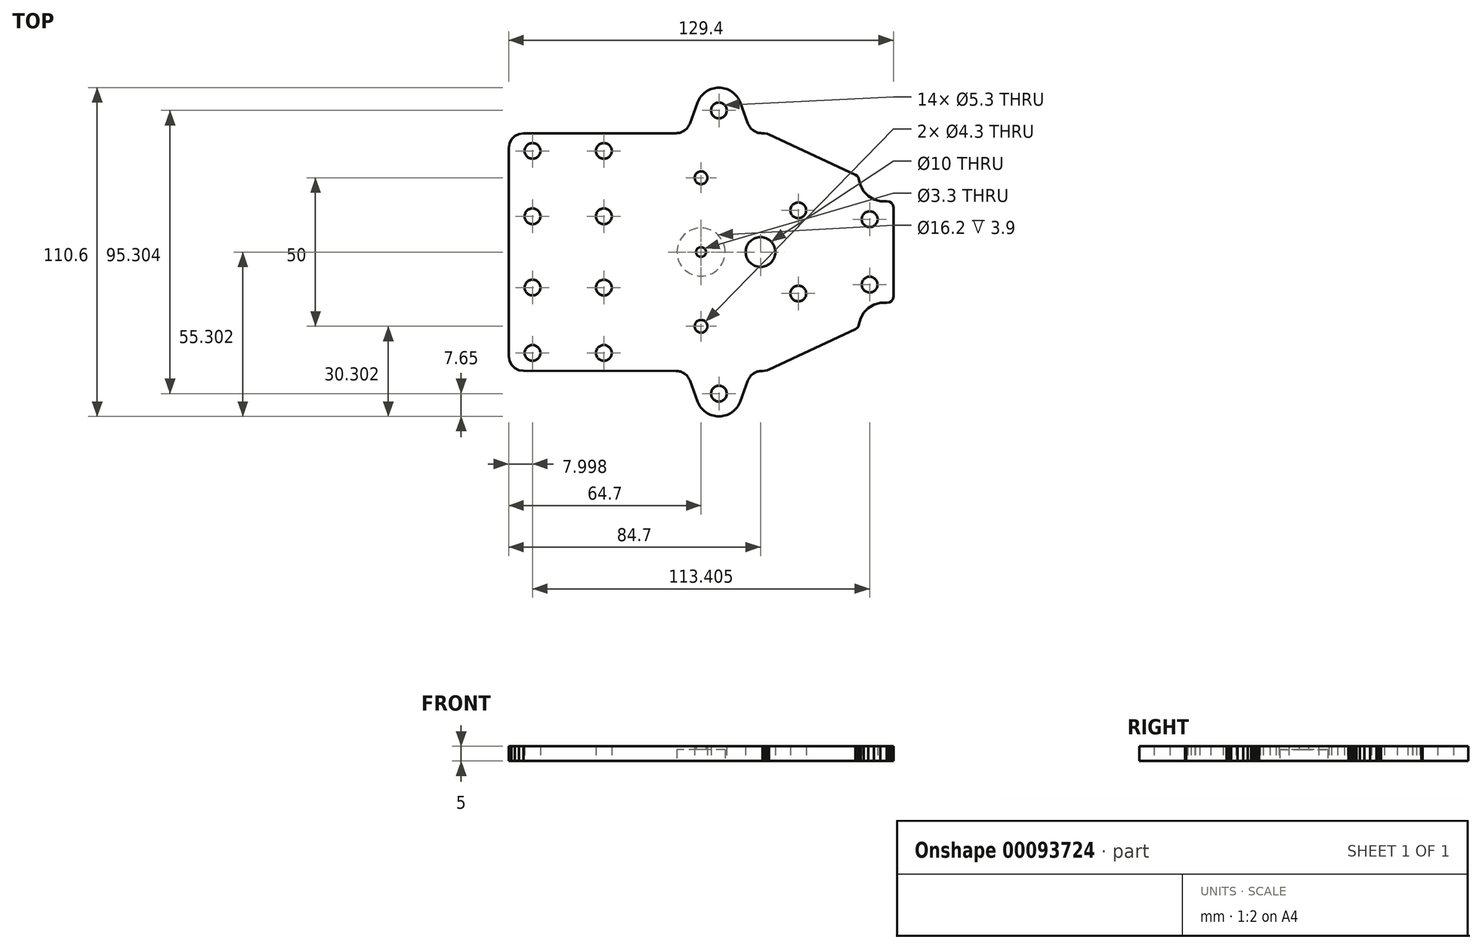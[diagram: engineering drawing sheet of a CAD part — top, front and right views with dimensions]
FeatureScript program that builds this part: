
annotation { "Feature Type Name" : "Feature", "Feature Type Description" : "" }
export const myFeature = defineFeature(function(context is Context, id is Id, definition is map)
    precondition{}
    {
        {
            var Q0;
            Q0=qCreatedBy(makeId("Top.planeOp"),FACE);
            var sketch = newSketch(context, id + "F0", { "sketchPlane" : qUnion([Q0])});
            skLineSegment(sketch, "E0", {"start": v(-58.76, 13.43) * mm, "end": v(-57.86, 14.22) * mm});
            skLineSegment(sketch, "E1", {"start": v(-57.86, 14.22) * mm, "end": v(-56.7, 14.5) * mm});
            skLineSegment(sketch, "E2", {"start": v(-56.7, 14.5) * mm, "end": v(-55.54, 14.21) * mm});
            skLineSegment(sketch, "E3", {"start": v(-55.54, 14.21) * mm, "end": v(-54.64, 13.42) * mm});
            skLineSegment(sketch, "E4", {"start": v(-54.64, 13.42) * mm, "end": v(-54.22, 12.3) * mm});
            skLineSegment(sketch, "E5", {"start": v(-54.22, 12.3) * mm, "end": v(-54.37, 11.12) * mm});
            skLineSegment(sketch, "E6", {"start": v(-54.37, 11.12) * mm, "end": v(-55.04, 10.13) * mm});
            skLineSegment(sketch, "E7", {"start": v(-55.04, 10.13) * mm, "end": v(-56.1, 9.57) * mm});
            skLineSegment(sketch, "E8", {"start": v(-56.1, 9.57) * mm, "end": v(-57.3, 9.58) * mm});
            skLineSegment(sketch, "E9", {"start": v(-57.3, 9.58) * mm, "end": v(-58.36, 10.13) * mm});
            skLineSegment(sketch, "E10", {"start": v(-58.36, 10.13) * mm, "end": v(-59.04, 11.12) * mm});
            skLineSegment(sketch, "E11", {"start": v(-59.04, 11.12) * mm, "end": v(-59.18, 12.3) * mm});
            skLineSegment(sketch, "E12", {"start": v(-59.18, 12.3) * mm, "end": v(-58.76, 13.43) * mm});
            skLineSegment(sketch, "E13", {"start": v(35.04, -14.88) * mm, "end": v(34.36, -15.87) * mm});
            skLineSegment(sketch, "E14", {"start": v(34.36, -15.87) * mm, "end": v(33.3, -16.43) * mm});
            skLineSegment(sketch, "E15", {"start": v(33.3, -16.43) * mm, "end": v(32.1, -16.42) * mm});
            skLineSegment(sketch, "E16", {"start": v(32.1, -16.42) * mm, "end": v(31.04, -15.87) * mm});
            skLineSegment(sketch, "E17", {"start": v(31.04, -15.87) * mm, "end": v(30.36, -14.89) * mm});
            skLineSegment(sketch, "E18", {"start": v(30.36, -14.89) * mm, "end": v(30.22, -13.7) * mm});
            skLineSegment(sketch, "E19", {"start": v(30.22, -13.7) * mm, "end": v(30.64, -12.57) * mm});
            skLineSegment(sketch, "E20", {"start": v(30.64, -12.57) * mm, "end": v(31.54, -11.79) * mm});
            skLineSegment(sketch, "E21", {"start": v(31.54, -11.79) * mm, "end": v(32.7, -11.5) * mm});
            skLineSegment(sketch, "E22", {"start": v(32.7, -11.5) * mm, "end": v(33.86, -11.79) * mm});
            skLineSegment(sketch, "E23", {"start": v(33.86, -11.79) * mm, "end": v(34.76, -12.58) * mm});
            skLineSegment(sketch, "E24", {"start": v(34.76, -12.58) * mm, "end": v(35.18, -13.7) * mm});
            skLineSegment(sketch, "E25", {"start": v(35.18, -13.7) * mm, "end": v(35.04, -14.88) * mm});
            skLineSegment(sketch, "E26", {"start": v(54.72, -20.36) * mm, "end": v(56.27, -18.8) * mm});
            skLineSegment(sketch, "E27", {"start": v(56.27, -18.8) * mm, "end": v(58.16, -17.68) * mm});
            skLineSegment(sketch, "E28", {"start": v(58.16, -17.68) * mm, "end": v(60.27, -17.08) * mm});
            skLineSegment(sketch, "E29", {"start": v(60.27, -17.08) * mm, "end": v(62.47, -17.06) * mm});
            skLineSegment(sketch, "E30", {"start": v(62.47, -17.06) * mm, "end": v(63.3, -16.97) * mm});
            skLineSegment(sketch, "E31", {"start": v(63.3, -16.97) * mm, "end": v(64.03, -16.56) * mm});
            skLineSegment(sketch, "E32", {"start": v(64.03, -16.56) * mm, "end": v(64.52, -15.88) * mm});
            skLineSegment(sketch, "E33", {"start": v(64.52, -15.88) * mm, "end": v(64.7, -15.07) * mm});
            skLineSegment(sketch, "E34", {"start": v(64.7, -15.07) * mm, "end": v(64.7, 15.07) * mm});
            skLineSegment(sketch, "E35", {"start": v(64.7, 15.07) * mm, "end": v(64.53, 15.9) * mm});
            skLineSegment(sketch, "E36", {"start": v(64.53, 15.9) * mm, "end": v(64.03, 16.57) * mm});
            skLineSegment(sketch, "E37", {"start": v(64.03, 16.57) * mm, "end": v(63.3, 16.98) * mm});
            skLineSegment(sketch, "E38", {"start": v(63.3, 16.98) * mm, "end": v(62.47, 17.06) * mm});
            skLineSegment(sketch, "E39", {"start": v(62.47, 17.06) * mm, "end": v(60.27, 17.08) * mm});
            skLineSegment(sketch, "E40", {"start": v(60.27, 17.08) * mm, "end": v(58.15, 17.68) * mm});
            skLineSegment(sketch, "E41", {"start": v(58.15, 17.68) * mm, "end": v(56.26, 18.8) * mm});
            skLineSegment(sketch, "E42", {"start": v(56.26, 18.8) * mm, "end": v(54.72, 20.36) * mm});
            skLineSegment(sketch, "E43", {"start": v(54.72, 20.36) * mm, "end": v(53.64, 22.28) * mm});
            skLineSegment(sketch, "E44", {"start": v(53.64, 22.28) * mm, "end": v(53.07, 24.4) * mm});
            skLineSegment(sketch, "E45", {"start": v(53.07, 24.4) * mm, "end": v(52.88, 25.04) * mm});
            skLineSegment(sketch, "E46", {"start": v(52.88, 25.04) * mm, "end": v(52.48, 25.58) * mm});
            skLineSegment(sketch, "E47", {"start": v(52.48, 25.58) * mm, "end": v(51.93, 25.95) * mm});
            skLineSegment(sketch, "E48", {"start": v(51.93, 25.95) * mm, "end": v(22.81, 39.53) * mm});
            skLineSegment(sketch, "E49", {"start": v(22.81, 39.53) * mm, "end": v(22.14, 39.8) * mm});
            skLineSegment(sketch, "E50", {"start": v(22.14, 39.8) * mm, "end": v(21.43, 39.95) * mm});
            skLineSegment(sketch, "E51", {"start": v(21.43, 39.95) * mm, "end": v(20.7, 40) * mm});
            skLineSegment(sketch, "E52", {"start": v(20.7, 40) * mm, "end": v(-59.7, 40) * mm});
            skLineSegment(sketch, "E53", {"start": v(-59.7, 40) * mm, "end": v(-61.24, 39.76) * mm});
            skLineSegment(sketch, "E54", {"start": v(-61.24, 39.76) * mm, "end": v(-62.63, 39.05) * mm});
            skLineSegment(sketch, "E55", {"start": v(-62.63, 39.05) * mm, "end": v(-63.75, 37.95) * mm});
            skLineSegment(sketch, "E56", {"start": v(-63.75, 37.95) * mm, "end": v(-64.45, 36.55) * mm});
            skLineSegment(sketch, "E57", {"start": v(-64.45, 36.55) * mm, "end": v(-64.7, 35) * mm});
            skLineSegment(sketch, "E58", {"start": v(-64.7, 35) * mm, "end": v(-64.7, -35) * mm});
            skLineSegment(sketch, "E59", {"start": v(-64.7, -35) * mm, "end": v(-64.45, -36.54) * mm});
            skLineSegment(sketch, "E60", {"start": v(-64.45, -36.54) * mm, "end": v(-63.75, -37.93) * mm});
            skLineSegment(sketch, "E61", {"start": v(-63.75, -37.93) * mm, "end": v(-62.63, -39.04) * mm});
            skLineSegment(sketch, "E62", {"start": v(-62.63, -39.04) * mm, "end": v(-61.25, -39.75) * mm});
            skLineSegment(sketch, "E63", {"start": v(-61.25, -39.75) * mm, "end": v(-59.7, -40) * mm});
            skLineSegment(sketch, "E64", {"start": v(-59.7, -40) * mm, "end": v(20.7, -40) * mm});
            skLineSegment(sketch, "E65", {"start": v(20.7, -40) * mm, "end": v(21.43, -39.95) * mm});
            skLineSegment(sketch, "E66", {"start": v(21.43, -39.95) * mm, "end": v(22.14, -39.8) * mm});
            skLineSegment(sketch, "E67", {"start": v(22.14, -39.8) * mm, "end": v(22.81, -39.53) * mm});
            skLineSegment(sketch, "E68", {"start": v(22.81, -39.53) * mm, "end": v(51.93, -25.95) * mm});
            skLineSegment(sketch, "E69", {"start": v(51.93, -25.95) * mm, "end": v(52.48, -25.57) * mm});
            skLineSegment(sketch, "E70", {"start": v(52.48, -25.57) * mm, "end": v(52.87, -25.04) * mm});
            skLineSegment(sketch, "E71", {"start": v(52.87, -25.04) * mm, "end": v(53.07, -24.4) * mm});
            skLineSegment(sketch, "E72", {"start": v(53.07, -24.4) * mm, "end": v(53.63, -22.27) * mm});
            skLineSegment(sketch, "E73", {"start": v(53.63, -22.27) * mm, "end": v(54.72, -20.36) * mm});
            skLineSegment(sketch, "E74", {"start": v(54.36, -11.89) * mm, "end": v(54.22, -10.7) * mm});
            skLineSegment(sketch, "E75", {"start": v(54.22, -10.7) * mm, "end": v(54.65, -9.58) * mm});
            skLineSegment(sketch, "E76", {"start": v(54.65, -9.58) * mm, "end": v(55.54, -8.79) * mm});
            skLineSegment(sketch, "E77", {"start": v(55.54, -8.79) * mm, "end": v(56.7, -8.5) * mm});
            skLineSegment(sketch, "E78", {"start": v(56.7, -8.5) * mm, "end": v(57.86, -8.78) * mm});
            skLineSegment(sketch, "E79", {"start": v(57.86, -8.78) * mm, "end": v(58.75, -9.57) * mm});
            skLineSegment(sketch, "E80", {"start": v(58.75, -9.57) * mm, "end": v(59.18, -10.7) * mm});
            skLineSegment(sketch, "E81", {"start": v(59.18, -10.7) * mm, "end": v(59.04, -11.89) * mm});
            skLineSegment(sketch, "E82", {"start": v(59.04, -11.89) * mm, "end": v(58.36, -12.87) * mm});
            skLineSegment(sketch, "E83", {"start": v(58.36, -12.87) * mm, "end": v(57.3, -13.42) * mm});
            skLineSegment(sketch, "E84", {"start": v(57.3, -13.42) * mm, "end": v(56.1, -13.42) * mm});
            skLineSegment(sketch, "E85", {"start": v(56.1, -13.42) * mm, "end": v(55.04, -12.87) * mm});
            skLineSegment(sketch, "E86", {"start": v(55.04, -12.87) * mm, "end": v(54.36, -11.89) * mm});
            skLineSegment(sketch, "E87", {"start": v(-30.64, -32.58) * mm, "end": v(-30.22, -33.7) * mm});
            skLineSegment(sketch, "E88", {"start": v(-30.22, -33.7) * mm, "end": v(-30.36, -34.89) * mm});
            skLineSegment(sketch, "E89", {"start": v(-30.36, -34.89) * mm, "end": v(-31.04, -35.87) * mm});
            skLineSegment(sketch, "E90", {"start": v(-31.04, -35.87) * mm, "end": v(-32.1, -36.43) * mm});
            skLineSegment(sketch, "E91", {"start": v(-32.1, -36.43) * mm, "end": v(-33.3, -36.42) * mm});
            skLineSegment(sketch, "E92", {"start": v(-33.3, -36.42) * mm, "end": v(-34.36, -35.87) * mm});
            skLineSegment(sketch, "E93", {"start": v(-34.36, -35.87) * mm, "end": v(-35.04, -34.88) * mm});
            skLineSegment(sketch, "E94", {"start": v(-35.04, -34.88) * mm, "end": v(-35.18, -33.7) * mm});
            skLineSegment(sketch, "E95", {"start": v(-35.18, -33.7) * mm, "end": v(-34.76, -32.57) * mm});
            skLineSegment(sketch, "E96", {"start": v(-34.76, -32.57) * mm, "end": v(-33.86, -31.79) * mm});
            skLineSegment(sketch, "E97", {"start": v(-33.86, -31.79) * mm, "end": v(-32.7, -31.5) * mm});
            skLineSegment(sketch, "E98", {"start": v(-32.7, -31.5) * mm, "end": v(-31.54, -31.78) * mm});
            skLineSegment(sketch, "E99", {"start": v(-31.54, -31.78) * mm, "end": v(-30.64, -32.58) * mm});
            skLineSegment(sketch, "E100", {"start": v(4.37, -36.83) * mm, "end": v(3.71, -35.87) * mm});
            skLineSegment(sketch, "E101", {"start": v(3.71, -35.87) * mm, "end": v(3.57, -34.7) * mm});
            skLineSegment(sketch, "E102", {"start": v(3.57, -34.7) * mm, "end": v(3.98, -33.6) * mm});
            skLineSegment(sketch, "E103", {"start": v(3.98, -33.6) * mm, "end": v(4.86, -32.83) * mm});
            skLineSegment(sketch, "E104", {"start": v(4.86, -32.83) * mm, "end": v(6, -32.55) * mm});
            skLineSegment(sketch, "E105", {"start": v(6, -32.55) * mm, "end": v(7.14, -32.83) * mm});
            skLineSegment(sketch, "E106", {"start": v(7.14, -32.83) * mm, "end": v(8.02, -33.6) * mm});
            skLineSegment(sketch, "E107", {"start": v(8.02, -33.6) * mm, "end": v(8.43, -34.7) * mm});
            skLineSegment(sketch, "E108", {"start": v(8.43, -34.7) * mm, "end": v(8.29, -35.86) * mm});
            skLineSegment(sketch, "E109", {"start": v(8.29, -35.86) * mm, "end": v(7.62, -36.83) * mm});
            skLineSegment(sketch, "E110", {"start": v(7.62, -36.83) * mm, "end": v(6.58, -37.37) * mm});
            skLineSegment(sketch, "E111", {"start": v(6.58, -37.37) * mm, "end": v(5.4, -37.38) * mm});
            skLineSegment(sketch, "E112", {"start": v(5.4, -37.38) * mm, "end": v(4.37, -36.83) * mm});
            skLineSegment(sketch, "E113", {"start": v(58.36, 9.13) * mm, "end": v(57.3, 8.58) * mm});
            skLineSegment(sketch, "E114", {"start": v(57.3, 8.58) * mm, "end": v(56.1, 8.58) * mm});
            skLineSegment(sketch, "E115", {"start": v(56.1, 8.58) * mm, "end": v(55.04, 9.13) * mm});
            skLineSegment(sketch, "E116", {"start": v(55.04, 9.13) * mm, "end": v(54.36, 10.12) * mm});
            skLineSegment(sketch, "E117", {"start": v(54.36, 10.12) * mm, "end": v(54.21, 11.3) * mm});
            skLineSegment(sketch, "E118", {"start": v(54.21, 11.3) * mm, "end": v(54.64, 12.42) * mm});
            skLineSegment(sketch, "E119", {"start": v(54.64, 12.42) * mm, "end": v(55.54, 13.21) * mm});
            skLineSegment(sketch, "E120", {"start": v(55.54, 13.21) * mm, "end": v(56.7, 13.5) * mm});
            skLineSegment(sketch, "E121", {"start": v(56.7, 13.5) * mm, "end": v(57.86, 13.22) * mm});
            skLineSegment(sketch, "E122", {"start": v(57.86, 13.22) * mm, "end": v(58.75, 12.42) * mm});
            skLineSegment(sketch, "E123", {"start": v(58.75, 12.42) * mm, "end": v(59.18, 11.3) * mm});
            skLineSegment(sketch, "E124", {"start": v(59.18, 11.3) * mm, "end": v(59.03, 10.11) * mm});
            skLineSegment(sketch, "E125", {"start": v(59.03, 10.11) * mm, "end": v(58.36, 9.13) * mm});
            skLineSegment(sketch, "E126", {"start": v(-30.21, 34.3) * mm, "end": v(-30.36, 33.11) * mm});
            skLineSegment(sketch, "E127", {"start": v(-30.36, 33.11) * mm, "end": v(-31.04, 32.13) * mm});
            skLineSegment(sketch, "E128", {"start": v(-31.04, 32.13) * mm, "end": v(-32.1, 31.58) * mm});
            skLineSegment(sketch, "E129", {"start": v(-32.1, 31.58) * mm, "end": v(-33.3, 31.58) * mm});
            skLineSegment(sketch, "E130", {"start": v(-33.3, 31.58) * mm, "end": v(-34.36, 32.13) * mm});
            skLineSegment(sketch, "E131", {"start": v(-34.36, 32.13) * mm, "end": v(-35.03, 33.12) * mm});
            skLineSegment(sketch, "E132", {"start": v(-35.03, 33.12) * mm, "end": v(-35.18, 34.3) * mm});
            skLineSegment(sketch, "E133", {"start": v(-35.18, 34.3) * mm, "end": v(-34.76, 35.42) * mm});
            skLineSegment(sketch, "E134", {"start": v(-34.76, 35.42) * mm, "end": v(-33.86, 36.21) * mm});
            skLineSegment(sketch, "E135", {"start": v(-33.86, 36.21) * mm, "end": v(-32.7, 36.5) * mm});
            skLineSegment(sketch, "E136", {"start": v(-32.7, 36.5) * mm, "end": v(-31.54, 36.21) * mm});
            skLineSegment(sketch, "E137", {"start": v(-31.54, 36.21) * mm, "end": v(-30.64, 35.42) * mm});
            skLineSegment(sketch, "E138", {"start": v(-30.64, 35.42) * mm, "end": v(-30.21, 34.3) * mm});
            skLineSegment(sketch, "E139", {"start": v(3.98, 36.4) * mm, "end": v(4.86, 37.17) * mm});
            skLineSegment(sketch, "E140", {"start": v(4.86, 37.17) * mm, "end": v(6, 37.45) * mm});
            skLineSegment(sketch, "E141", {"start": v(6, 37.45) * mm, "end": v(7.14, 37.17) * mm});
            skLineSegment(sketch, "E142", {"start": v(7.14, 37.17) * mm, "end": v(8.02, 36.39) * mm});
            skLineSegment(sketch, "E143", {"start": v(8.02, 36.39) * mm, "end": v(8.43, 35.3) * mm});
            skLineSegment(sketch, "E144", {"start": v(8.43, 35.3) * mm, "end": v(8.3, 34.13) * mm});
            skLineSegment(sketch, "E145", {"start": v(8.3, 34.13) * mm, "end": v(7.62, 33.17) * mm});
            skLineSegment(sketch, "E146", {"start": v(7.62, 33.17) * mm, "end": v(6.58, 32.63) * mm});
            skLineSegment(sketch, "E147", {"start": v(6.58, 32.63) * mm, "end": v(5.4, 32.62) * mm});
            skLineSegment(sketch, "E148", {"start": v(5.4, 32.62) * mm, "end": v(4.37, 33.17) * mm});
            skLineSegment(sketch, "E149", {"start": v(4.37, 33.17) * mm, "end": v(3.7, 34.13) * mm});
            skLineSegment(sketch, "E150", {"start": v(3.7, 34.13) * mm, "end": v(3.57, 35.3) * mm});
            skLineSegment(sketch, "E151", {"start": v(3.57, 35.3) * mm, "end": v(3.98, 36.4) * mm});
            skLineSegment(sketch, "E152", {"start": v(-54.64, -32.58) * mm, "end": v(-54.22, -33.7) * mm});
            skLineSegment(sketch, "E153", {"start": v(-54.22, -33.7) * mm, "end": v(-54.36, -34.89) * mm});
            skLineSegment(sketch, "E154", {"start": v(-54.36, -34.89) * mm, "end": v(-55.04, -35.87) * mm});
            skLineSegment(sketch, "E155", {"start": v(-55.04, -35.87) * mm, "end": v(-56.1, -36.42) * mm});
            skLineSegment(sketch, "E156", {"start": v(-56.1, -36.42) * mm, "end": v(-57.3, -36.42) * mm});
            skLineSegment(sketch, "E157", {"start": v(-57.3, -36.42) * mm, "end": v(-58.36, -35.87) * mm});
            skLineSegment(sketch, "E158", {"start": v(-58.36, -35.87) * mm, "end": v(-59.04, -34.88) * mm});
            skLineSegment(sketch, "E159", {"start": v(-59.04, -34.88) * mm, "end": v(-59.18, -33.7) * mm});
            skLineSegment(sketch, "E160", {"start": v(-59.18, -33.7) * mm, "end": v(-58.76, -32.57) * mm});
            skLineSegment(sketch, "E161", {"start": v(-58.76, -32.57) * mm, "end": v(-57.86, -31.79) * mm});
            skLineSegment(sketch, "E162", {"start": v(-57.86, -31.79) * mm, "end": v(-56.7, -31.5) * mm});
            skLineSegment(sketch, "E163", {"start": v(-56.7, -31.5) * mm, "end": v(-55.53, -31.78) * mm});
            skLineSegment(sketch, "E164", {"start": v(-55.53, -31.78) * mm, "end": v(-54.64, -32.58) * mm});
            skLineSegment(sketch, "E165", {"start": v(-56.1, -14.43) * mm, "end": v(-57.3, -14.42) * mm});
            skLineSegment(sketch, "E166", {"start": v(-57.3, -14.42) * mm, "end": v(-58.36, -13.87) * mm});
            skLineSegment(sketch, "E167", {"start": v(-58.36, -13.87) * mm, "end": v(-59.04, -12.89) * mm});
            skLineSegment(sketch, "E168", {"start": v(-59.04, -12.89) * mm, "end": v(-59.18, -11.7) * mm});
            skLineSegment(sketch, "E169", {"start": v(-59.18, -11.7) * mm, "end": v(-58.76, -10.57) * mm});
            skLineSegment(sketch, "E170", {"start": v(-58.76, -10.57) * mm, "end": v(-57.86, -9.78) * mm});
            skLineSegment(sketch, "E171", {"start": v(-57.86, -9.78) * mm, "end": v(-56.7, -9.5) * mm});
            skLineSegment(sketch, "E172", {"start": v(-56.7, -9.5) * mm, "end": v(-55.54, -9.79) * mm});
            skLineSegment(sketch, "E173", {"start": v(-55.54, -9.79) * mm, "end": v(-54.65, -10.58) * mm});
            skLineSegment(sketch, "E174", {"start": v(-54.65, -10.58) * mm, "end": v(-54.22, -11.7) * mm});
            skLineSegment(sketch, "E175", {"start": v(-54.22, -11.7) * mm, "end": v(-54.36, -12.89) * mm});
            skLineSegment(sketch, "E176", {"start": v(-54.36, -12.89) * mm, "end": v(-55.04, -13.87) * mm});
            skLineSegment(sketch, "E177", {"start": v(-55.04, -13.87) * mm, "end": v(-56.1, -14.43) * mm});
            skLineSegment(sketch, "E178", {"start": v(-56.1, 31.57) * mm, "end": v(-57.3, 31.57) * mm});
            skLineSegment(sketch, "E179", {"start": v(-57.3, 31.57) * mm, "end": v(-58.35, 32.13) * mm});
            skLineSegment(sketch, "E180", {"start": v(-58.35, 32.13) * mm, "end": v(-59.04, 33.11) * mm});
            skLineSegment(sketch, "E181", {"start": v(-59.04, 33.11) * mm, "end": v(-59.18, 34.3) * mm});
            skLineSegment(sketch, "E182", {"start": v(-59.18, 34.3) * mm, "end": v(-58.76, 35.42) * mm});
            skLineSegment(sketch, "E183", {"start": v(-58.76, 35.42) * mm, "end": v(-57.86, 36.21) * mm});
            skLineSegment(sketch, "E184", {"start": v(-57.86, 36.21) * mm, "end": v(-56.7, 36.5) * mm});
            skLineSegment(sketch, "E185", {"start": v(-56.7, 36.5) * mm, "end": v(-55.54, 36.21) * mm});
            skLineSegment(sketch, "E186", {"start": v(-55.54, 36.21) * mm, "end": v(-54.64, 35.42) * mm});
            skLineSegment(sketch, "E187", {"start": v(-54.64, 35.42) * mm, "end": v(-54.22, 34.3) * mm});
            skLineSegment(sketch, "E188", {"start": v(-54.22, 34.3) * mm, "end": v(-54.36, 33.11) * mm});
            skLineSegment(sketch, "E189", {"start": v(-54.36, 33.11) * mm, "end": v(-55.04, 32.13) * mm});
            skLineSegment(sketch, "E190", {"start": v(-55.04, 32.13) * mm, "end": v(-56.1, 31.57) * mm});
            skLineSegment(sketch, "E191", {"start": v(-30.36, -12.89) * mm, "end": v(-31.04, -13.87) * mm});
            skLineSegment(sketch, "E192", {"start": v(-31.04, -13.87) * mm, "end": v(-32.1, -14.43) * mm});
            skLineSegment(sketch, "E193", {"start": v(-32.1, -14.43) * mm, "end": v(-33.3, -14.42) * mm});
            skLineSegment(sketch, "E194", {"start": v(-33.3, -14.42) * mm, "end": v(-34.36, -13.87) * mm});
            skLineSegment(sketch, "E195", {"start": v(-34.36, -13.87) * mm, "end": v(-35.03, -12.88) * mm});
            skLineSegment(sketch, "E196", {"start": v(-35.03, -12.88) * mm, "end": v(-35.18, -11.7) * mm});
            skLineSegment(sketch, "E197", {"start": v(-35.18, -11.7) * mm, "end": v(-34.76, -10.58) * mm});
            skLineSegment(sketch, "E198", {"start": v(-34.76, -10.58) * mm, "end": v(-33.86, -9.78) * mm});
            skLineSegment(sketch, "E199", {"start": v(-33.86, -9.78) * mm, "end": v(-32.7, -9.5) * mm});
            skLineSegment(sketch, "E200", {"start": v(-32.7, -9.5) * mm, "end": v(-31.54, -9.79) * mm});
            skLineSegment(sketch, "E201", {"start": v(-31.54, -9.79) * mm, "end": v(-30.64, -10.58) * mm});
            skLineSegment(sketch, "E202", {"start": v(-30.64, -10.58) * mm, "end": v(-30.22, -11.7) * mm});
            skLineSegment(sketch, "E203", {"start": v(-30.22, -11.7) * mm, "end": v(-30.36, -12.89) * mm});
            skLineSegment(sketch, "E204", {"start": v(-33.86, 14.21) * mm, "end": v(-32.7, 14.5) * mm});
            skLineSegment(sketch, "E205", {"start": v(-32.7, 14.5) * mm, "end": v(-31.54, 14.21) * mm});
            skLineSegment(sketch, "E206", {"start": v(-31.54, 14.21) * mm, "end": v(-30.64, 13.43) * mm});
            skLineSegment(sketch, "E207", {"start": v(-30.64, 13.43) * mm, "end": v(-30.22, 12.3) * mm});
            skLineSegment(sketch, "E208", {"start": v(-30.22, 12.3) * mm, "end": v(-30.36, 11.12) * mm});
            skLineSegment(sketch, "E209", {"start": v(-30.36, 11.12) * mm, "end": v(-31.04, 10.13) * mm});
            skLineSegment(sketch, "E210", {"start": v(-31.04, 10.13) * mm, "end": v(-32.1, 9.58) * mm});
            skLineSegment(sketch, "E211", {"start": v(-32.1, 9.58) * mm, "end": v(-33.3, 9.58) * mm});
            skLineSegment(sketch, "E212", {"start": v(-33.3, 9.58) * mm, "end": v(-34.35, 10.13) * mm});
            skLineSegment(sketch, "E213", {"start": v(-34.35, 10.13) * mm, "end": v(-35.04, 11.12) * mm});
            skLineSegment(sketch, "E214", {"start": v(-35.04, 11.12) * mm, "end": v(-35.18, 12.3) * mm});
            skLineSegment(sketch, "E215", {"start": v(-35.18, 12.3) * mm, "end": v(-34.76, 13.43) * mm});
            skLineSegment(sketch, "E216", {"start": v(-34.76, 13.43) * mm, "end": v(-33.86, 14.21) * mm});
            skLineSegment(sketch, "E217", {"start": v(33.86, 16.21) * mm, "end": v(34.75, 15.42) * mm});
            skLineSegment(sketch, "E218", {"start": v(34.75, 15.42) * mm, "end": v(35.18, 14.3) * mm});
            skLineSegment(sketch, "E219", {"start": v(35.18, 14.3) * mm, "end": v(35.04, 13.11) * mm});
            skLineSegment(sketch, "E220", {"start": v(35.04, 13.11) * mm, "end": v(34.35, 12.13) * mm});
            skLineSegment(sketch, "E221", {"start": v(34.35, 12.13) * mm, "end": v(33.3, 11.57) * mm});
            skLineSegment(sketch, "E222", {"start": v(33.3, 11.57) * mm, "end": v(32.1, 11.57) * mm});
            skLineSegment(sketch, "E223", {"start": v(32.1, 11.57) * mm, "end": v(31.04, 12.13) * mm});
            skLineSegment(sketch, "E224", {"start": v(31.04, 12.13) * mm, "end": v(30.36, 13.12) * mm});
            skLineSegment(sketch, "E225", {"start": v(30.36, 13.12) * mm, "end": v(30.22, 14.3) * mm});
            skLineSegment(sketch, "E226", {"start": v(30.22, 14.3) * mm, "end": v(30.64, 15.42) * mm});
            skLineSegment(sketch, "E227", {"start": v(30.64, 15.42) * mm, "end": v(31.54, 16.21) * mm});
            skLineSegment(sketch, "E228", {"start": v(31.54, 16.21) * mm, "end": v(32.7, 16.5) * mm});
            skLineSegment(sketch, "E229", {"start": v(32.7, 16.5) * mm, "end": v(33.86, 16.21) * mm});
            skSolve(sketch);
        }
        {
            var Q0;
            Q0=qCreatedBy(makeId("Top.planeOp"),FACE);
            var sketch = newSketch(context, id + "F1", { "sketchPlane" : qUnion([Q0])});
            skLineSegment(sketch, "E230.0", {"start": v(-64.7, 35) * mm, "end": v(-64.7, -35) * mm});
            skLineSegment(sketch, "E230.1", {"start": v(20.7, 40) * mm, "end": v(16.98, 40) * mm});
            skLineSegment(sketch, "E230.2", {"start": v(51.93, 25.95) * mm, "end": v(22.81, 39.53) * mm});
            skLineSegment(sketch, "E230.3", {"start": v(64.7, -15.07) * mm, "end": v(64.7, 15.07) * mm});
            skLineSegment(sketch, "E230.4", {"start": v(22.81, -39.53) * mm, "end": v(51.93, -25.95) * mm});
            skLineSegment(sketch, "E230.5", {"start": v(-59.7, -40) * mm, "end": v(-4.98, -40) * mm});
            skLineSegment(sketch, "E231.0", {"start": v(20.7, -40) * mm, "end": v(21.43, -39.95) * mm});
            skLineSegment(sketch, "E231.1", {"start": v(21.43, -39.95) * mm, "end": v(22.14, -39.8) * mm});
            skLineSegment(sketch, "E231.2", {"start": v(22.14, -39.8) * mm, "end": v(22.81, -39.53) * mm});
            skLineSegment(sketch, "E232.0", {"start": v(51.93, -25.95) * mm, "end": v(52.48, -25.57) * mm});
            skLineSegment(sketch, "E232.1", {"start": v(52.48, -25.57) * mm, "end": v(52.87, -25.04) * mm});
            skLineSegment(sketch, "E232.2", {"start": v(52.87, -25.04) * mm, "end": v(53.07, -24.4) * mm});
            skLineSegment(sketch, "E232.3", {"start": v(53.07, -24.4) * mm, "end": v(53.63, -22.27) * mm});
            skLineSegment(sketch, "E232.4", {"start": v(53.63, -22.27) * mm, "end": v(54.72, -20.36) * mm});
            skLineSegment(sketch, "E232.5", {"start": v(54.72, -20.36) * mm, "end": v(56.27, -18.8) * mm});
            skLineSegment(sketch, "E232.6", {"start": v(58.16, -17.68) * mm, "end": v(60.27, -17.08) * mm});
            skLineSegment(sketch, "E232.7", {"start": v(56.27, -18.8) * mm, "end": v(58.16, -17.68) * mm});
            skLineSegment(sketch, "E232.8", {"start": v(60.27, -17.08) * mm, "end": v(62.47, -17.06) * mm});
            skLineSegment(sketch, "E232.9", {"start": v(62.47, -17.06) * mm, "end": v(63.3, -16.97) * mm});
            skLineSegment(sketch, "E232.10", {"start": v(63.3, -16.97) * mm, "end": v(64.03, -16.56) * mm});
            skLineSegment(sketch, "E232.11", {"start": v(64.03, -16.56) * mm, "end": v(64.52, -15.88) * mm});
            skLineSegment(sketch, "E232.12", {"start": v(64.52, -15.88) * mm, "end": v(64.7, -15.07) * mm});
            skLineSegment(sketch, "E233.0", {"start": v(64.7, 15.07) * mm, "end": v(64.53, 15.9) * mm});
            skLineSegment(sketch, "E233.1", {"start": v(64.53, 15.9) * mm, "end": v(64.03, 16.57) * mm});
            skLineSegment(sketch, "E233.2", {"start": v(64.03, 16.57) * mm, "end": v(63.3, 16.98) * mm});
            skLineSegment(sketch, "E233.3", {"start": v(63.3, 16.98) * mm, "end": v(62.47, 17.06) * mm});
            skLineSegment(sketch, "E233.4", {"start": v(62.47, 17.06) * mm, "end": v(60.27, 17.08) * mm});
            skLineSegment(sketch, "E233.5", {"start": v(60.27, 17.08) * mm, "end": v(58.15, 17.68) * mm});
            skLineSegment(sketch, "E233.6", {"start": v(58.15, 17.68) * mm, "end": v(56.26, 18.8) * mm});
            skLineSegment(sketch, "E233.7", {"start": v(56.26, 18.8) * mm, "end": v(54.72, 20.36) * mm});
            skLineSegment(sketch, "E233.8", {"start": v(54.72, 20.36) * mm, "end": v(53.64, 22.28) * mm});
            skLineSegment(sketch, "E233.9", {"start": v(53.64, 22.28) * mm, "end": v(53.07, 24.4) * mm});
            skLineSegment(sketch, "E233.10", {"start": v(53.07, 24.4) * mm, "end": v(52.88, 25.04) * mm});
            skLineSegment(sketch, "E233.11", {"start": v(52.88, 25.04) * mm, "end": v(52.48, 25.58) * mm});
            skLineSegment(sketch, "E233.12", {"start": v(52.48, 25.58) * mm, "end": v(51.93, 25.95) * mm});
            skLineSegment(sketch, "E234.0", {"start": v(22.81, 39.53) * mm, "end": v(22.14, 39.8) * mm});
            skLineSegment(sketch, "E234.1", {"start": v(22.14, 39.8) * mm, "end": v(21.43, 39.95) * mm});
            skLineSegment(sketch, "E234.2", {"start": v(21.43, 39.95) * mm, "end": v(20.7, 40) * mm});
            skLineSegment(sketch, "E235.0", {"start": v(-64.45, 36.55) * mm, "end": v(-64.7, 35) * mm});
            skLineSegment(sketch, "E235.1", {"start": v(-63.75, 37.95) * mm, "end": v(-64.45, 36.55) * mm});
            skLineSegment(sketch, "E235.2", {"start": v(-62.63, 39.05) * mm, "end": v(-63.75, 37.95) * mm});
            skLineSegment(sketch, "E235.3", {"start": v(-61.24, 39.76) * mm, "end": v(-62.63, 39.05) * mm});
            skLineSegment(sketch, "E235.4", {"start": v(-59.7, 40) * mm, "end": v(-61.24, 39.76) * mm});
            skLineSegment(sketch, "E236.0", {"start": v(-64.7, -35) * mm, "end": v(-64.45, -36.54) * mm});
            skLineSegment(sketch, "E236.1", {"start": v(-64.45, -36.54) * mm, "end": v(-63.75, -37.93) * mm});
            skLineSegment(sketch, "E236.2", {"start": v(-63.75, -37.93) * mm, "end": v(-62.63, -39.04) * mm});
            skLineSegment(sketch, "E236.3", {"start": v(-62.63, -39.04) * mm, "end": v(-61.25, -39.75) * mm});
            skLineSegment(sketch, "E236.4", {"start": v(-61.25, -39.75) * mm, "end": v(-59.7, -40) * mm});
            skLineSegment(sketch, "E237.0.0", {"start": v(-54.22, -33.7) * mm, "end": v(-54.64, -32.58) * mm, "construction": true});
            skLineSegment(sketch, "E237.0.1", {"start": v(-54.64, -32.58) * mm, "end": v(-55.53, -31.78) * mm, "construction": true});
            skLineSegment(sketch, "E237.0.2", {"start": v(-55.53, -31.78) * mm, "end": v(-56.7, -31.5) * mm, "construction": true});
            skLineSegment(sketch, "E237.0.3", {"start": v(-56.7, -31.5) * mm, "end": v(-57.86, -31.79) * mm, "construction": true});
            skLineSegment(sketch, "E237.0.4", {"start": v(-57.86, -31.79) * mm, "end": v(-58.76, -32.57) * mm, "construction": true});
            skLineSegment(sketch, "E237.0.5", {"start": v(-58.76, -32.57) * mm, "end": v(-59.18, -33.7) * mm, "construction": true});
            skLineSegment(sketch, "E237.0.6", {"start": v(-59.18, -33.7) * mm, "end": v(-59.04, -34.88) * mm, "construction": true});
            skLineSegment(sketch, "E237.0.7", {"start": v(-59.04, -34.88) * mm, "end": v(-58.36, -35.87) * mm, "construction": true});
            skLineSegment(sketch, "E237.0.8", {"start": v(-58.36, -35.87) * mm, "end": v(-57.3, -36.42) * mm, "construction": true});
            skLineSegment(sketch, "E237.0.9", {"start": v(-57.3, -36.42) * mm, "end": v(-56.1, -36.42) * mm, "construction": true});
            skLineSegment(sketch, "E237.0.10", {"start": v(-56.1, -36.42) * mm, "end": v(-55.04, -35.87) * mm, "construction": true});
            skLineSegment(sketch, "E237.0.11", {"start": v(-55.04, -35.87) * mm, "end": v(-54.36, -34.89) * mm, "construction": true});
            skLineSegment(sketch, "E237.0.12", {"start": v(-54.36, -34.89) * mm, "end": v(-54.22, -33.7) * mm, "construction": true});
            skLineSegment(sketch, "E238", {"start": v(-56.7, -31.5) * mm, "end": v(-56.7, -36.42) * mm, "construction": true});
            skCircle(sketch, "E239", {"center": v(-56.7, -33.96) * mm, "radius": 2.65 * mm});
            skLineSegment(sketch, "E240.0", {"start": v(-33.86, -31.79) * mm, "end": v(-32.7, -31.5) * mm, "construction": true});
            skLineSegment(sketch, "E240.1", {"start": v(-32.7, -31.5) * mm, "end": v(-31.54, -31.78) * mm, "construction": true});
            skLineSegment(sketch, "E241.0", {"start": v(-32.1, -36.43) * mm, "end": v(-33.3, -36.42) * mm, "construction": true});
            skLineSegment(sketch, "E242", {"start": v(-32.7, -31.5) * mm, "end": v(-32.7, -36.42) * mm, "construction": true});
            skCircle(sketch, "E243", {"center": v(-32.7, -33.96) * mm, "radius": 2.65 * mm});
            skLineSegment(sketch, "E244.0", {"start": v(4.86, 37.17) * mm, "end": v(6, 37.45) * mm, "construction": true});
            skLineSegment(sketch, "E244.1", {"start": v(6, 37.45) * mm, "end": v(7.14, 37.17) * mm, "construction": true});
            skLineSegment(sketch, "E244.2", {"start": v(6.58, 32.63) * mm, "end": v(5.4, 32.62) * mm, "construction": true});
            skLineSegment(sketch, "E245", {"start": v(6, 37.45) * mm, "end": v(6, 32.62) * mm, "construction": true});
            skLineSegment(sketch, "E246.0", {"start": v(4.86, -32.83) * mm, "end": v(6, -32.55) * mm, "construction": true});
            skLineSegment(sketch, "E246.1", {"start": v(6, -32.55) * mm, "end": v(7.14, -32.83) * mm, "construction": true});
            skLineSegment(sketch, "E246.2", {"start": v(6.58, -37.37) * mm, "end": v(5.4, -37.38) * mm, "construction": true});
            skLineSegment(sketch, "E247", {"start": v(6, -32.55) * mm, "end": v(6, -63) * mm, "construction": true});
            skCircle(sketch, "E248", {"center": v(6, -47.65) * mm, "radius": 2.65 * mm});
            skLineSegment(sketch, "E249", {"start": v(6, -40) * mm, "end": v(15.97, -40) * mm, "construction": true});
            skLineSegment(sketch, "E250.MirrorCS", {"start": v(-3.97, -40) * mm, "end": v(-3.97, -40) * mm});
            skArc(sketch, "E251", {"start": v(-1.39, -49.63) * mm, "mid": v(-1.3, -49.97) * mm, "end": v(-1.18, -50.3) * mm, "construction": true});
            skArc(sketch, "E252", {"start": v(13.39, -49.63) * mm, "mid": v(6, -40) * mm, "end": v(-1.39, -49.63) * mm, "construction": true});
            skLineSegment(sketch, "E253", {"start": v(15.97, -40) * mm, "end": v(16.98, -40) * mm, "construction": true});
            skLineSegment(sketch, "E254", {"start": v(-3.96, -40) * mm, "end": v(6, -40) * mm, "construction": true});
            skLineSegment(sketch, "E255.0", {"start": v(-57.86, -9.78) * mm, "end": v(-56.7, -9.5) * mm});
            skLineSegment(sketch, "E256.0", {"start": v(-56.7, -9.5) * mm, "end": v(-55.54, -9.79) * mm});
            skLineSegment(sketch, "E257.0", {"start": v(-57.86, 14.22) * mm, "end": v(-56.7, 14.5) * mm, "construction": true});
            skLineSegment(sketch, "E258.0", {"start": v(-56.7, 14.5) * mm, "end": v(-55.54, 14.21) * mm, "construction": true});
            skLineSegment(sketch, "E259.0", {"start": v(-33.86, 14.21) * mm, "end": v(-32.7, 14.5) * mm});
            skLineSegment(sketch, "E260.0", {"start": v(-32.7, 14.5) * mm, "end": v(-31.54, 14.21) * mm});
            skLineSegment(sketch, "E261.0", {"start": v(-32.1, 9.58) * mm, "end": v(-33.3, 9.58) * mm});
            skLineSegment(sketch, "E262.0", {"start": v(-56.1, 9.57) * mm, "end": v(-57.3, 9.58) * mm, "construction": true});
            skLineSegment(sketch, "E263.0", {"start": v(-56.1, -14.43) * mm, "end": v(-57.3, -14.42) * mm});
            skLineSegment(sketch, "E264.0", {"start": v(-32.1, -14.43) * mm, "end": v(-33.3, -14.42) * mm});
            skLineSegment(sketch, "E265.0", {"start": v(-32.7, -9.5) * mm, "end": v(-31.54, -9.79) * mm});
            skLineSegment(sketch, "E265.1", {"start": v(-33.86, -9.78) * mm, "end": v(-32.7, -9.5) * mm});
            skLineSegment(sketch, "E266", {"start": v(-56.7, 14.5) * mm, "end": v(-56.7, 9.58) * mm, "construction": true});
            skLineSegment(sketch, "E267", {"start": v(-32.7, 14.5) * mm, "end": v(-32.7, 9.58) * mm, "construction": true});
            skLineSegment(sketch, "E268", {"start": v(-32.7, -9.5) * mm, "end": v(-32.7, -14.43) * mm, "construction": true});
            skLineSegment(sketch, "E269", {"start": v(-56.7, -9.5) * mm, "end": v(-56.7, -14.42) * mm, "construction": true});
            skLineSegment(sketch, "E270.0", {"start": v(-57.86, 36.21) * mm, "end": v(-56.7, 36.5) * mm});
            skLineSegment(sketch, "E270.1", {"start": v(-56.7, 36.5) * mm, "end": v(-55.54, 36.21) * mm});
            skLineSegment(sketch, "E270.2", {"start": v(-56.1, 31.57) * mm, "end": v(-57.3, 31.57) * mm});
            skLineSegment(sketch, "E270.3", {"start": v(-33.86, 36.21) * mm, "end": v(-32.7, 36.5) * mm});
            skLineSegment(sketch, "E270.4", {"start": v(-32.7, 36.5) * mm, "end": v(-31.54, 36.21) * mm});
            skLineSegment(sketch, "E270.5", {"start": v(-32.1, 31.58) * mm, "end": v(-33.3, 31.58) * mm});
            skLineSegment(sketch, "E271", {"start": v(-56.7, 36.5) * mm, "end": v(-56.7, 31.57) * mm, "construction": true});
            skLineSegment(sketch, "E272", {"start": v(-32.7, 36.5) * mm, "end": v(-32.7, 31.58) * mm, "construction": true});
            skLineSegment(sketch, "E273.0", {"start": v(31.54, 16.21) * mm, "end": v(32.7, 16.5) * mm});
            skLineSegment(sketch, "E273.1", {"start": v(32.7, 16.5) * mm, "end": v(33.86, 16.21) * mm});
            skLineSegment(sketch, "E273.2", {"start": v(33.3, 11.57) * mm, "end": v(32.1, 11.57) * mm});
            skLineSegment(sketch, "E273.3", {"start": v(55.54, 13.21) * mm, "end": v(56.7, 13.5) * mm});
            skLineSegment(sketch, "E273.4", {"start": v(56.7, 13.5) * mm, "end": v(57.86, 13.22) * mm});
            skLineSegment(sketch, "E273.5", {"start": v(57.3, 8.58) * mm, "end": v(56.1, 8.58) * mm});
            skLineSegment(sketch, "E273.6", {"start": v(31.54, -11.79) * mm, "end": v(32.7, -11.5) * mm});
            skLineSegment(sketch, "E273.7", {"start": v(32.7, -11.5) * mm, "end": v(33.86, -11.79) * mm});
            skLineSegment(sketch, "E273.8", {"start": v(33.3, -16.43) * mm, "end": v(32.1, -16.42) * mm});
            skLineSegment(sketch, "E273.9", {"start": v(55.54, -8.79) * mm, "end": v(56.7, -8.5) * mm});
            skLineSegment(sketch, "E273.10", {"start": v(56.7, -8.5) * mm, "end": v(57.86, -8.78) * mm});
            skLineSegment(sketch, "E273.11", {"start": v(57.3, -13.42) * mm, "end": v(56.1, -13.42) * mm});
            skLineSegment(sketch, "E274", {"start": v(32.7, -11.5) * mm, "end": v(32.7, -16.43) * mm, "construction": true});
            skLineSegment(sketch, "E275", {"start": v(56.7, -8.5) * mm, "end": v(56.7, -13.42) * mm, "construction": true});
            skLineSegment(sketch, "E276", {"start": v(56.7, 13.5) * mm, "end": v(56.7, 8.58) * mm, "construction": true});
            skLineSegment(sketch, "E277", {"start": v(32.7, 16.5) * mm, "end": v(32.7, 11.57) * mm, "construction": true});
            skCircle(sketch, "E278", {"center": v(32.7, 14.04) * mm, "radius": 2.65 * mm});
            skCircle(sketch, "E279", {"center": v(56.7, 11.04) * mm, "radius": 2.65 * mm});
            skCircle(sketch, "E280", {"center": v(32.7, -13.96) * mm, "radius": 2.65 * mm});
            skCircle(sketch, "E281", {"center": v(56.7, -10.96) * mm, "radius": 2.65 * mm});
            skCircle(sketch, "E282", {"center": v(-32.7, 34.04) * mm, "radius": 2.65 * mm});
            skCircle(sketch, "E283", {"center": v(-56.7, 34.04) * mm, "radius": 2.65 * mm});
            skCircle(sketch, "E284", {"center": v(-56.7, 12.04) * mm, "radius": 2.65 * mm});
            skCircle(sketch, "E285", {"center": v(-32.7, 12.04) * mm, "radius": 2.65 * mm});
            skCircle(sketch, "E286", {"center": v(-56.7, -11.96) * mm, "radius": 2.65 * mm});
            skCircle(sketch, "E287", {"center": v(-32.7, -11.96) * mm, "radius": 2.65 * mm});
            skLineSegment(sketch, "E288", {"start": v(-64.7, 0) * mm, "end": v(64.7, 0) * mm, "construction": true});
            skLineSegment(sketch, "E289", {"start": v(0, 0) * mm, "end": v(0, 40) * mm, "construction": true});
            skCircle(sketch, "E290", {"center": v(0, 0) * mm, "radius": 1.65 * mm});
            skCircle(sketch, "E291", {"center": v(0, 0) * mm, "radius": 8.1 * mm});
            skCircle(sketch, "E292", {"center": v(0, 25) * mm, "radius": 2.15 * mm});
            skCircle(sketch, "E293.MirrorC", {"center": v(0, -25) * mm, "radius": 2.15 * mm});
            skCircle(sketch, "E294", {"center": v(20, 0) * mm, "radius": 5 * mm});
            skLineSegment(sketch, "E295.MirrorCS", {"start": v(6, -40) * mm, "end": v(-3.97, -40) * mm, "construction": true});
            skLineSegment(sketch, "E296", {"start": v(-1.18, -50.3) * mm, "end": v(6, -50.3) * mm, "construction": true});
            skLineSegment(sketch, "E297", {"start": v(13.18, -50.3) * mm, "end": v(16.98, -40) * mm});
            skArc(sketch, "E298", {"start": v(13.18, -50.3) * mm, "mid": v(13.3, -49.97) * mm, "end": v(13.39, -49.63) * mm, "construction": true});
            skLineSegment(sketch, "E299", {"start": v(6, -50.3) * mm, "end": v(13.18, -50.3) * mm, "construction": true});
            skArc(sketch, "E300", {"start": v(-1.18, -50.3) * mm, "mid": v(6, -55.3) * mm, "end": v(13.18, -50.3) * mm});
            skLineSegment(sketch, "E301", {"start": v(16.98, -40) * mm, "end": v(20.7, -40) * mm});
            skLineSegment(sketch, "E302", {"start": v(-1.18, -50.3) * mm, "end": v(-4.98, -40) * mm});
            skLineSegment(sketch, "E303", {"start": v(-4.98, -40) * mm, "end": v(-3.96, -40) * mm, "construction": true});
            skArc(sketch, "E304.MirrorCS", {"start": v(-1.18, 50.3) * mm, "mid": v(6, 55.3) * mm, "end": v(13.18, 50.3) * mm});
            skCircle(sketch, "E305.MirrorC", {"center": v(6, 47.65) * mm, "radius": 2.65 * mm});
            skLineSegment(sketch, "E306", {"start": v(13.18, 50.3) * mm, "end": v(16.98, 40) * mm});
            skLineSegment(sketch, "E307", {"start": v(-1.18, 50.3) * mm, "end": v(-4.98, 40) * mm});
            skLineSegment(sketch, "E308", {"start": v(-4.98, 40) * mm, "end": v(-59.7, 40) * mm});
            skLineSegment(sketch, "E309", {"start": v(16.98, 40) * mm, "end": v(-4.98, 40) * mm, "construction": true});
            skSolve(sketch);
        }
        {
            var Q0;
            Q0=makeQuery(id+"F1.imprint","IMPRINT",FACE,{"disambiguationData":[TD([[makeQuery(id+"F1.imprint","IMPRINT",EDGE,{"derivedFrom":sQuery(id+"F1.wireOp",EDGE,"E230.0")}),1.0]])]});
            var Q1;
            Q1=makeQuery(id+"F1.imprint","IMPRINT",FACE,{"disambiguationData":[TD([[makeQuery(id+"F1.imprint","IMPRINT",EDGE,{"derivedFrom":sQuery(id+"F1.wireOp",EDGE,"E290")}),-1.0]])]});
            extrude(context, id + "F2", {"entities" : qUnion([Q0, Q1]), "depth" : 5 * mm});
        }
        {
            var Q0;
            Q0=makeQuery(id+"F1.imprint","IMPRINT",FACE,{"disambiguationData":[TD([[makeQuery(id+"F1.imprint","IMPRINT",EDGE,{"derivedFrom":sQuery(id+"F1.wireOp",EDGE,"E290")}),-1.0]])]});
            extrude(context, id + "F3", {"entities" : qUnion([Q0]), "operationType" : NewBodyOperationType.REMOVE, "depth" : 3.9 * mm});
        }
        {
            var Q0;
            Q0=makeQuery(id+"F2.opExtrude","SWEPT_EDGE",EDGE,{"disambiguationData":[OSD([sQuery(id+"F1.wireOp",EDGE,"E230.5"),sQuery(id+"F1.wireOp",EDGE,"E302")])]});
            var Q1;
            Q1=makeQuery(id+"F2.opExtrude","SWEPT_EDGE",EDGE,{"disambiguationData":[OSD([sQuery(id+"F1.wireOp",EDGE,"E297"),sQuery(id+"F1.wireOp",EDGE,"E301")])]});
            var Q2;
            Q2=makeQuery(id+"F2.opExtrude","SWEPT_EDGE",EDGE,{"disambiguationData":[OSD([sQuery(id+"F1.wireOp",EDGE,"E307"),sQuery(id+"F1.wireOp",EDGE,"E308")])]});
            var Q3;
            Q3=makeQuery(id+"F2.opExtrude","SWEPT_EDGE",EDGE,{"disambiguationData":[OSD([sQuery(id+"F1.wireOp",EDGE,"E230.1"),sQuery(id+"F1.wireOp",EDGE,"E306")])]});
            fillet(context, id + "F4", {"entities" : qUnion([Q0, Q1, Q2, Q3]), "radius" : 5 * mm, "tangentPropagation" : true, "allowEdgeOverflow" : false});
        }
    });
